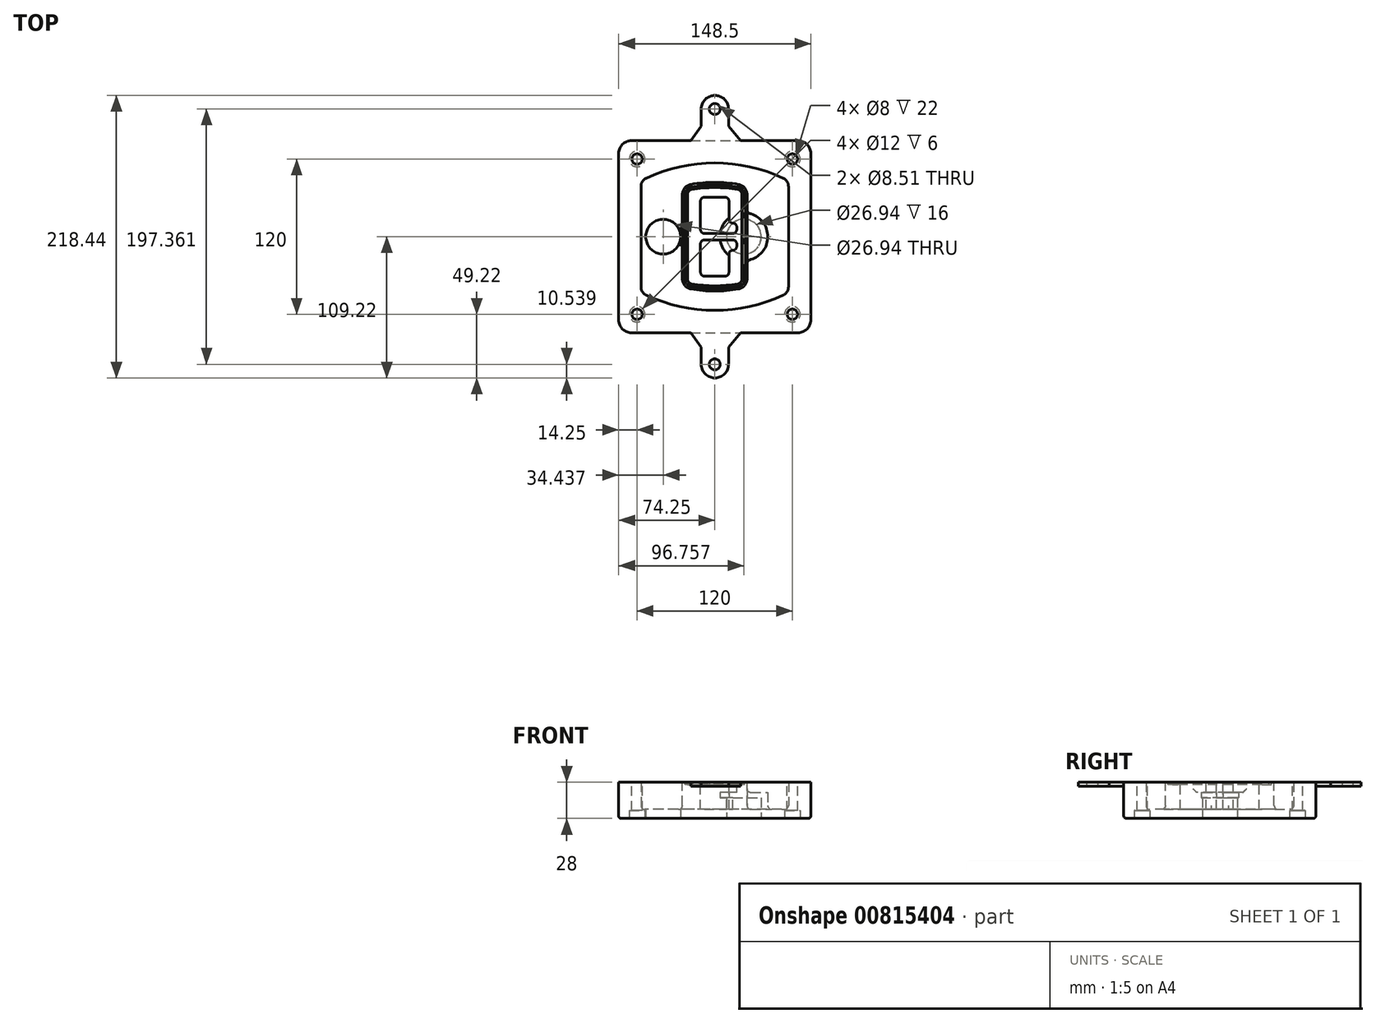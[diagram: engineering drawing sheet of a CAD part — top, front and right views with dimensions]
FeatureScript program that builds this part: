
annotation { "Feature Type Name" : "Feature", "Feature Type Description" : "" }
export const myFeature = defineFeature(function(context is Context, id is Id, definition is map)
    precondition{}
    {
        {
            var Q0;
            Q0=qCreatedBy(makeId("Top.planeOp"),FACE);
            var sketch = newSketch(context, id + "F0", { "sketchPlane" : qUnion([Q0])});
            skPoint(sketch, "E0.rect.middle", {"position": v(0, 0) * mm});
            skLineSegment(sketch, "E1.bottom", {"start": v(-64.25, -74.25) * mm, "end": v(64.25, -74.25) * mm});
            skLineSegment(sketch, "E1.top", {"start": v(-64.25, 74.25) * mm, "end": v(64.25, 74.25) * mm});
            skLineSegment(sketch, "E1.left", {"start": v(-74.25, -64.25) * mm, "end": v(-74.25, 64.25) * mm});
            skLineSegment(sketch, "E1.right", {"start": v(74.25, -64.25) * mm, "end": v(74.25, 64.25) * mm});
            skLineSegment(sketch, "E2", {"start": v(-74.25, 74.25) * mm, "end": v(74.25, -74.25) * mm, "construction": true});
            skLineSegment(sketch, "E3", {"start": v(74.25, 74.25) * mm, "end": v(-74.25, -74.25) * mm, "construction": true});
            skCircle(sketch, "E4", {"center": v(-60, 60) * mm, "radius": 4 * mm});
            skCircle(sketch, "E5", {"center": v(60, 60) * mm, "radius": 4 * mm});
            skCircle(sketch, "E6", {"center": v(60, -60) * mm, "radius": 4 * mm});
            skCircle(sketch, "E7", {"center": v(-60, -60) * mm, "radius": 4 * mm});
            skLineSegment(sketch, "E8", {"start": v(-60, 60) * mm, "end": v(60, 60) * mm, "construction": true});
            skLineSegment(sketch, "E9", {"start": v(60, 60) * mm, "end": v(60, -60) * mm, "construction": true});
            skLineSegment(sketch, "E10", {"start": v(60, -60) * mm, "end": v(-60, -60) * mm, "construction": true});
            skLineSegment(sketch, "E11", {"start": v(-60, -60) * mm, "end": v(-60, 60) * mm, "construction": true});
            skLineSegment(sketch, "E12", {"start": v(-60, 38.83) * mm, "end": v(-60, -38.83) * mm});
            skLineSegment(sketch, "E13", {"start": v(60, 38.83) * mm, "end": v(60, -38.83) * mm});
            skArc(sketch, "E14", {"start": v(54.26, 47.88) * mm, "mid": v(0, 60) * mm, "end": v(-54.26, 47.88) * mm});
            skArc(sketch, "E15", {"start": v(-54.26, -47.88) * mm, "mid": v(0, -60) * mm, "end": v(54.26, -47.88) * mm});
            skLineSegment(sketch, "E16", {"start": v(-60, 0) * mm, "end": v(60, 0) * mm, "construction": true});
            skPoint(sketch, "E17.visualSharp", {"position": v(-60, -45) * mm});
            skArc(sketch, "E17.filletArc", {"start": v(-60, -38.83) * mm, "mid": v(-58.44, -44.2) * mm, "end": v(-54.26, -47.88) * mm});
            skPoint(sketch, "E18.visualSharp", {"position": v(-60, 45) * mm});
            skArc(sketch, "E18.filletArc", {"start": v(-54.26, 47.88) * mm, "mid": v(-58.44, 44.2) * mm, "end": v(-60, 38.83) * mm});
            skPoint(sketch, "E19.visualSharp", {"position": v(60, 45) * mm});
            skArc(sketch, "E19.filletArc", {"start": v(60, 38.83) * mm, "mid": v(58.44, 44.2) * mm, "end": v(54.26, 47.88) * mm});
            skPoint(sketch, "E20.visualSharp", {"position": v(60, -45) * mm});
            skArc(sketch, "E20.filletArc", {"start": v(54.26, -47.88) * mm, "mid": v(58.44, -44.2) * mm, "end": v(60, -38.83) * mm});
            skPoint(sketch, "E21.visualSharp", {"position": v(-74.25, 74.25) * mm});
            skArc(sketch, "E21.filletArc", {"start": v(-64.25, 74.25) * mm, "mid": v(-71.32, 71.32) * mm, "end": v(-74.25, 64.25) * mm});
            skPoint(sketch, "E22.visualSharp", {"position": v(74.25, 74.25) * mm});
            skArc(sketch, "E22.filletArc", {"start": v(74.25, 64.25) * mm, "mid": v(71.32, 71.32) * mm, "end": v(64.25, 74.25) * mm});
            skPoint(sketch, "E23.visualSharp", {"position": v(74.25, -74.25) * mm});
            skArc(sketch, "E23.filletArc", {"start": v(64.25, -74.25) * mm, "mid": v(71.32, -71.32) * mm, "end": v(74.25, -64.25) * mm});
            skPoint(sketch, "E24.visualSharp", {"position": v(-74.25, -74.25) * mm});
            skArc(sketch, "E24.filletArc", {"start": v(-74.25, -64.25) * mm, "mid": v(-71.32, -71.32) * mm, "end": v(-64.25, -74.25) * mm});
            skArc(sketch, "E25.0", {"start": v(57, 38.83) * mm, "mid": v(55.9, 42.58) * mm, "end": v(52.98, 45.17) * mm});
            skLineSegment(sketch, "E25.1", {"start": v(57, 38.83) * mm, "end": v(57, -38.83) * mm});
            skArc(sketch, "E25.2", {"start": v(52.98, -45.17) * mm, "mid": v(55.9, -42.58) * mm, "end": v(57, -38.83) * mm});
            skArc(sketch, "E25.3", {"start": v(-52.98, -45.17) * mm, "mid": v(0, -57) * mm, "end": v(52.98, -45.17) * mm});
            skArc(sketch, "E25.4", {"start": v(-57, -38.83) * mm, "mid": v(-55.9, -42.58) * mm, "end": v(-52.98, -45.17) * mm});
            skArc(sketch, "E25.5", {"start": v(52.98, 45.17) * mm, "mid": v(0, 57) * mm, "end": v(-52.98, 45.17) * mm});
            skLineSegment(sketch, "E25.6", {"start": v(-57, 38.83) * mm, "end": v(-57, -38.83) * mm});
            skArc(sketch, "E25.7", {"start": v(-52.98, 45.17) * mm, "mid": v(-55.9, 42.58) * mm, "end": v(-57, 38.83) * mm});
            skArc(sketch, "E26.0", {"start": v(-55.96, 51.5) * mm, "mid": v(-61.82, 46.33) * mm, "end": v(-64, 38.83) * mm});
            skArc(sketch, "E26.1", {"start": v(55.96, 51.5) * mm, "mid": v(0, 64) * mm, "end": v(-55.96, 51.5) * mm});
            skArc(sketch, "E26.2", {"start": v(64, 38.83) * mm, "mid": v(61.82, 46.33) * mm, "end": v(55.96, 51.5) * mm});
            skLineSegment(sketch, "E26.3", {"start": v(64, 38.83) * mm, "end": v(64, -38.83) * mm});
            skArc(sketch, "E26.4", {"start": v(55.96, -51.5) * mm, "mid": v(61.82, -46.33) * mm, "end": v(64, -38.83) * mm});
            skLineSegment(sketch, "E26.5", {"start": v(-64, 38.83) * mm, "end": v(-64, -38.83) * mm});
            skArc(sketch, "E26.6", {"start": v(-55.96, -51.5) * mm, "mid": v(0, -64) * mm, "end": v(55.96, -51.5) * mm});
            skArc(sketch, "E26.7", {"start": v(-64, -38.83) * mm, "mid": v(-61.82, -46.33) * mm, "end": v(-55.96, -51.5) * mm});
            skSolve(sketch);
        }
        {
            var Q0;
            Q0=makeQuery(id+"F0.imprint","IMPRINT",FACE,{"disambiguationData":[TD([[makeQuery(id+"F0.imprint","IMPRINT",EDGE,{"derivedFrom":sQuery(id+"F0.wireOp",EDGE,"E1.bottom")}),1.0]])]});
            var Q1;
            Q1=makeQuery(id+"F0.imprint","IMPRINT",FACE,{"disambiguationData":[TD([[makeQuery(id+"F0.imprint","IMPRINT",EDGE,{"derivedFrom":sQuery(id+"F0.wireOp",EDGE,"E12")}),1.0]])]});
            var Q2;
            Q2=makeQuery(id+"F0.imprint","IMPRINT",FACE,{"disambiguationData":[TD([[makeQuery(id+"F0.imprint","IMPRINT",EDGE,{"derivedFrom":sQuery(id+"F0.wireOp",EDGE,"E25.0")}),1.0]])]});
            var Q3;
            Q3=makeQuery(id+"F0.imprint","IMPRINT",FACE,{"disambiguationData":[TD([[makeQuery(id+"F0.imprint","IMPRINT",EDGE,{"derivedFrom":sQuery(id+"F0.wireOp",EDGE,"E12")}),-1.0]])]});
            extrude(context, id + "F1", {"entities" : qUnion([Q0, Q1, Q2, Q3]), "oppositeDirection" : true, "depth" : 25 * mm, "offsetDistance" : 25 * mm});
        }
        {
            var Q0;
            Q0=makeQuery(id+"F0.imprint","IMPRINT",FACE,{"disambiguationData":[TD([[makeQuery(id+"F0.imprint","IMPRINT",EDGE,{"derivedFrom":sQuery(id+"F0.wireOp",EDGE,"E12")}),1.0]])]});
            extrude(context, id + "F2", {"entities" : qUnion([Q0]), "operationType" : NewBodyOperationType.ADD, "depth" : 3 * mm});
        }
        {
            var Q0;
            Q0=makeQuery(id+"F0.imprint","IMPRINT",FACE,{"disambiguationData":[TD([[makeQuery(id+"F0.imprint","IMPRINT",EDGE,{"derivedFrom":sQuery(id+"F0.wireOp",EDGE,"E25.0")}),1.0]])]});
            extrude(context, id + "F3", {"entities" : qUnion([Q0]), "operationType" : NewBodyOperationType.REMOVE, "oppositeDirection" : true, "depth" : 18 * mm});
        }
        {
            var Q0;
            Q0=makeQuery(id+"F2.opExtrude","CAP_FACE",FACE,{"disambiguationData":[OSD([sQuery(id+"F0.wireOp",EDGE,"E12"),sQuery(id+"F0.wireOp",EDGE,"E13"),sQuery(id+"F0.wireOp",EDGE,"E14"),sQuery(id+"F0.wireOp",EDGE,"E15"),sQuery(id+"F0.wireOp",EDGE,"E17.filletArc"),sQuery(id+"F0.wireOp",EDGE,"E18.filletArc"),sQuery(id+"F0.wireOp",EDGE,"E19.filletArc"),sQuery(id+"F0.wireOp",EDGE,"E20.filletArc"),sQuery(id+"F0.wireOp",EDGE,"E25.0"),sQuery(id+"F0.wireOp",EDGE,"E25.1"),sQuery(id+"F0.wireOp",EDGE,"E25.2"),sQuery(id+"F0.wireOp",EDGE,"E25.3"),sQuery(id+"F0.wireOp",EDGE,"E25.4"),sQuery(id+"F0.wireOp",EDGE,"E25.5"),sQuery(id+"F0.wireOp",EDGE,"E25.6"),sQuery(id+"F0.wireOp",EDGE,"E25.7")])],"isStart":false});
            var sketch = newSketch(context, id + "F4", { "sketchPlane" : qUnion([Q0])});
            skArc(sketch, "E27.0", {"start": v(-18.34, -40.45) * mm, "mid": v(0, -42) * mm, "end": v(18.34, -40.45) * mm});
            skArc(sketch, "E28.0", {"start": v(18.34, 40.45) * mm, "mid": v(0, 42) * mm, "end": v(-18.34, 40.45) * mm});
            skLineSegment(sketch, "E29", {"start": v(-25, 32.57) * mm, "end": v(-25, -32.57) * mm});
            skLineSegment(sketch, "E30", {"start": v(25, 32.57) * mm, "end": v(25, -32.57) * mm});
            skLineSegment(sketch, "E31", {"start": v(-25, 39.1) * mm, "end": v(25, 39.1) * mm, "construction": true});
            skLineSegment(sketch, "E32", {"start": v(-25, -39.1) * mm, "end": v(25, -39.1) * mm, "construction": true});
            skPoint(sketch, "E33.visualSharp", {"position": v(-25, 39.1) * mm});
            skArc(sketch, "E33.filletArc", {"start": v(-18.34, 40.45) * mm, "mid": v(-23.11, 37.73) * mm, "end": v(-25, 32.57) * mm});
            skPoint(sketch, "E34.visualSharp", {"position": v(25, 39.1) * mm});
            skArc(sketch, "E34.filletArc", {"start": v(25, 32.57) * mm, "mid": v(23.11, 37.73) * mm, "end": v(18.34, 40.45) * mm});
            skPoint(sketch, "E35.visualSharp", {"position": v(25, -39.1) * mm});
            skArc(sketch, "E35.filletArc", {"start": v(18.34, -40.45) * mm, "mid": v(23.11, -37.73) * mm, "end": v(25, -32.57) * mm});
            skPoint(sketch, "E36.visualSharp", {"position": v(-25, -39.1) * mm});
            skArc(sketch, "E36.filletArc", {"start": v(-25, -32.57) * mm, "mid": v(-23.11, -37.73) * mm, "end": v(-18.34, -40.45) * mm});
            skArc(sketch, "E37.0", {"start": v(52.98, 45.17) * mm, "mid": v(0, 57) * mm, "end": v(-52.98, 45.17) * mm});
            skArc(sketch, "E37.1", {"start": v(-52.98, 45.17) * mm, "mid": v(-55.9, 42.58) * mm, "end": v(-57, 38.83) * mm});
            skLineSegment(sketch, "E37.2", {"start": v(-57, 38.83) * mm, "end": v(-57, -38.83) * mm});
            skArc(sketch, "E37.3", {"start": v(-57, -38.83) * mm, "mid": v(-55.9, -42.58) * mm, "end": v(-52.98, -45.17) * mm});
            skArc(sketch, "E37.4", {"start": v(-52.98, -45.17) * mm, "mid": v(0, -57) * mm, "end": v(52.98, -45.17) * mm});
            skArc(sketch, "E37.5", {"start": v(52.98, -45.17) * mm, "mid": v(55.9, -42.58) * mm, "end": v(57, -38.83) * mm});
            skLineSegment(sketch, "E37.6", {"start": v(57, 38.83) * mm, "end": v(57, -38.83) * mm});
            skArc(sketch, "E37.7", {"start": v(57, 38.83) * mm, "mid": v(55.9, 42.58) * mm, "end": v(52.98, 45.17) * mm});
            skLineSegment(sketch, "E38.0", {"start": v(23, 32.57) * mm, "end": v(23, -32.57) * mm});
            skArc(sketch, "E38.1", {"start": v(18, -38.48) * mm, "mid": v(21.58, -36.44) * mm, "end": v(23, -32.57) * mm});
            skArc(sketch, "E38.2", {"start": v(-18, -38.48) * mm, "mid": v(0, -40) * mm, "end": v(18, -38.48) * mm});
            skArc(sketch, "E38.3", {"start": v(-23, -32.57) * mm, "mid": v(-21.58, -36.44) * mm, "end": v(-18, -38.48) * mm});
            skLineSegment(sketch, "E38.4", {"start": v(-23, 32.57) * mm, "end": v(-23, -32.57) * mm});
            skArc(sketch, "E38.5", {"start": v(23, 32.57) * mm, "mid": v(21.58, 36.44) * mm, "end": v(18, 38.48) * mm});
            skArc(sketch, "E38.6", {"start": v(-18, 38.48) * mm, "mid": v(-21.58, 36.44) * mm, "end": v(-23, 32.57) * mm});
            skArc(sketch, "E38.7", {"start": v(18, 38.48) * mm, "mid": v(0, 40) * mm, "end": v(-18, 38.48) * mm});
            skArc(sketch, "E39.0", {"start": v(21, 32.57) * mm, "mid": v(20.06, 35.15) * mm, "end": v(17.67, 36.5) * mm});
            skLineSegment(sketch, "E39.1", {"start": v(21, 32.57) * mm, "end": v(21, -32.57) * mm});
            skArc(sketch, "E39.2", {"start": v(17.67, -36.5) * mm, "mid": v(20.06, -35.15) * mm, "end": v(21, -32.57) * mm});
            skArc(sketch, "E39.3", {"start": v(-17.67, -36.5) * mm, "mid": v(0, -38) * mm, "end": v(17.67, -36.5) * mm});
            skArc(sketch, "E39.4", {"start": v(-21, -32.57) * mm, "mid": v(-20.06, -35.15) * mm, "end": v(-17.67, -36.5) * mm});
            skArc(sketch, "E39.5", {"start": v(17.67, 36.5) * mm, "mid": v(0, 38) * mm, "end": v(-17.67, 36.5) * mm});
            skLineSegment(sketch, "E39.6", {"start": v(-21, 32.57) * mm, "end": v(-21, -32.57) * mm});
            skArc(sketch, "E39.7", {"start": v(-17.67, 36.5) * mm, "mid": v(-20.06, 35.15) * mm, "end": v(-21, 32.57) * mm});
            skLineSegment(sketch, "E40", {"start": v(-25, 0) * mm, "end": v(25, 0) * mm, "construction": true});
            skLineSegment(sketch, "E41", {"start": v(-11, 5.5) * mm, "end": v(-11, 27.5) * mm});
            skLineSegment(sketch, "E42", {"start": v(-8, 30.5) * mm, "end": v(8, 30.5) * mm});
            skLineSegment(sketch, "E43", {"start": v(11, 27.5) * mm, "end": v(11, 13.5) * mm});
            skLineSegment(sketch, "E44", {"start": v(14, 10.5) * mm, "end": v(14, 10.5) * mm});
            skLineSegment(sketch, "E45", {"start": v(17, 7.5) * mm, "end": v(17, 5.5) * mm});
            skLineSegment(sketch, "E46", {"start": v(14, 2.5) * mm, "end": v(-8, 2.5) * mm});
            skPoint(sketch, "E47.visualSharp", {"position": v(-11, 30.5) * mm});
            skArc(sketch, "E47.filletArc", {"start": v(-8, 30.5) * mm, "mid": v(-10.12, 29.62) * mm, "end": v(-11, 27.5) * mm});
            skPoint(sketch, "E48.visualSharp", {"position": v(11, 30.5) * mm});
            skArc(sketch, "E48.filletArc", {"start": v(11, 27.5) * mm, "mid": v(10.12, 29.62) * mm, "end": v(8, 30.5) * mm});
            skPoint(sketch, "E49.visualSharp", {"position": v(11, 10.5) * mm});
            skArc(sketch, "E49.filletArc", {"start": v(11, 13.5) * mm, "mid": v(11.88, 11.38) * mm, "end": v(14, 10.5) * mm});
            skPoint(sketch, "E50.visualSharp", {"position": v(17, 10.5) * mm});
            skArc(sketch, "E50.filletArc", {"start": v(17, 7.5) * mm, "mid": v(16.12, 9.62) * mm, "end": v(14, 10.5) * mm});
            skPoint(sketch, "E51.visualSharp", {"position": v(17, 2.5) * mm});
            skArc(sketch, "E51.filletArc", {"start": v(14, 2.5) * mm, "mid": v(16.12, 3.38) * mm, "end": v(17, 5.5) * mm});
            skPoint(sketch, "E52.visualSharp", {"position": v(-11, 2.5) * mm});
            skArc(sketch, "E52.filletArc", {"start": v(-11, 5.5) * mm, "mid": v(-10.12, 3.38) * mm, "end": v(-8, 2.5) * mm});
            skLineSegment(sketch, "E53.0.MirrorCS", {"start": v(14, -2.5) * mm, "end": v(-8, -2.5) * mm});
            skArc(sketch, "E54.0.MirrorCS", {"start": v(-11, -5.5) * mm, "mid": v(-10.12, -3.38) * mm, "end": v(-8, -2.5) * mm});
            skLineSegment(sketch, "E55.0.MirrorCS", {"start": v(-11, -5.5) * mm, "end": v(-11, -27.5) * mm});
            skArc(sketch, "E56.0.MirrorCS", {"start": v(-8, -30.5) * mm, "mid": v(-10.12, -29.62) * mm, "end": v(-11, -27.5) * mm});
            skLineSegment(sketch, "E57.0.MirrorCS", {"start": v(-8, -30.5) * mm, "end": v(8, -30.5) * mm});
            skArc(sketch, "E58.0.MirrorCS", {"start": v(11, -27.5) * mm, "mid": v(10.12, -29.62) * mm, "end": v(8, -30.5) * mm});
            skLineSegment(sketch, "E59.0.MirrorCS", {"start": v(11, -27.5) * mm, "end": v(11, -13.5) * mm});
            skArc(sketch, "E60.0.MirrorCS", {"start": v(11, -13.5) * mm, "mid": v(11.88, -11.38) * mm, "end": v(14, -10.5) * mm});
            skArc(sketch, "E61.0.MirrorCS", {"start": v(17, -7.5) * mm, "mid": v(16.12, -9.62) * mm, "end": v(14, -10.5) * mm});
            skLineSegment(sketch, "E62.0.MirrorCS", {"start": v(17, -7.5) * mm, "end": v(17, -5.5) * mm});
            skArc(sketch, "E63.0.MirrorCS", {"start": v(14, -2.5) * mm, "mid": v(16.12, -3.38) * mm, "end": v(17, -5.5) * mm});
            skSolve(sketch);
        }
        {
            var Q0;
            Q0=makeQuery(id+"F4.imprint","IMPRINT",FACE,{"disambiguationData":[TD([[makeQuery(id+"F4.imprint","IMPRINT",EDGE,{"derivedFrom":sQuery(id+"F4.wireOp",EDGE,"E27.0")}),1.0]])]});
            var Q1;
            Q1=makeQuery(id+"F4.imprint","IMPRINT",FACE,{"disambiguationData":[TD([[makeQuery(id+"F4.imprint","IMPRINT",EDGE,{"derivedFrom":sQuery(id+"F4.wireOp",EDGE,"E38.0")}),-1.0]])]});
            var Q2;
            Q2=makeQuery(id+"F4.imprint","IMPRINT",FACE,{"disambiguationData":[TD([[makeQuery(id+"F4.imprint","IMPRINT",EDGE,{"derivedFrom":sQuery(id+"F4.wireOp",EDGE,"E39.0")}),1.0]])]});
            extrude(context, id + "F5", {"entities" : qUnion([Q0, Q1, Q2]), "operationType" : NewBodyOperationType.ADD, "endBound" : BoundingType.UP_TO_NEXT, "oppositeDirection" : true, "depth" : 25 * mm, "offsetDistance" : 25 * mm});
        }
        {
            var Q0;
            Q0=makeQuery(id+"F4.imprint","IMPRINT",FACE,{"disambiguationData":[TD([[makeQuery(id+"F4.imprint","IMPRINT",EDGE,{"derivedFrom":sQuery(id+"F4.wireOp",EDGE,"E38.0")}),-1.0]])]});
            extrude(context, id + "F6", {"entities" : qUnion([Q0]), "operationType" : NewBodyOperationType.REMOVE, "oppositeDirection" : true, "depth" : 2 * mm});
        }
        {
            var Q0;
            Q0=makeQuery(id+"F1.opExtrude","CAP_FACE",FACE,{"disambiguationData":[OSD([sQuery(id+"F0.wireOp",EDGE,"E1.bottom"),sQuery(id+"F0.wireOp",EDGE,"E1.top"),sQuery(id+"F0.wireOp",EDGE,"E1.left"),sQuery(id+"F0.wireOp",EDGE,"E1.right"),sQuery(id+"F0.wireOp",EDGE,"E4"),sQuery(id+"F0.wireOp",EDGE,"E5"),sQuery(id+"F0.wireOp",EDGE,"E6"),sQuery(id+"F0.wireOp",EDGE,"E7"),sQuery(id+"F0.wireOp",EDGE,"E21.filletArc"),sQuery(id+"F0.wireOp",EDGE,"E22.filletArc"),sQuery(id+"F0.wireOp",EDGE,"E23.filletArc"),sQuery(id+"F0.wireOp",EDGE,"E24.filletArc")])],"isStart":false});
            var sketch = newSketch(context, id + "F7", { "sketchPlane" : qUnion([Q0])});
            skCircle(sketch, "E64", {"center": v(22.5, 0) * mm, "radius": 13.47 * mm});
            skCircle(sketch, "E65", {"center": v(-39.81, 0) * mm, "radius": 13.47 * mm});
            skLineSegment(sketch, "E66", {"start": v(74.25, 0) * mm, "end": v(-74.25, 0) * mm});
            skCircle(sketch, "E67", {"center": v(22.5, 0) * mm, "radius": 18.47 * mm});
            skCircle(sketch, "E68", {"center": v(60, -60) * mm, "radius": 6 * mm});
            skCircle(sketch, "E69", {"center": v(-60, -60) * mm, "radius": 6 * mm});
            skCircle(sketch, "E70", {"center": v(-60, 60) * mm, "radius": 6 * mm});
            skCircle(sketch, "E71", {"center": v(60, 60) * mm, "radius": 6 * mm});
            skSolve(sketch);
        }
        {
            var Q0;
            {var subQ1=sQuery(id+"F7.wireOp",EDGE,"E66");var subQ4=sQuery(id+"F7.wireOp",EDGE,"E64");var subQ6=makeQuery(id+"F7.imprint","INTERSECT",VERTEX,{"disambiguationData":[OD(0.0)],"derivedFrom":[subQ4,subQ1]});Q0=makeQuery(id+"F7.imprint","IMPRINT",FACE,{"disambiguationData":[TD([[makeQuery(id+"F7.imprint","IMPRINT",EDGE,{"disambiguationData":[TD([[subQ6,-1.0]])],"derivedFrom":subQ4}),-1.0]])]});}
            var Q1;
            {var subQ0=sQuery(id+"F7.wireOp",EDGE,"E66");var subQ1=sQuery(id+"F7.wireOp",EDGE,"E64");var subQ3=makeQuery(id+"F7.imprint","INTERSECT",VERTEX,{"disambiguationData":[OD(0.0)],"derivedFrom":[subQ1,subQ0]});Q1=makeQuery(id+"F7.imprint","IMPRINT",FACE,{"disambiguationData":[TD([[makeQuery(id+"F7.imprint","IMPRINT",EDGE,{"disambiguationData":[TD([[subQ3,-1.0]])],"derivedFrom":subQ1}),1.0]])]});}
            var Q2;
            {var subQ0=sQuery(id+"F7.wireOp",EDGE,"E66");var subQ1=sQuery(id+"F7.wireOp",EDGE,"E64");var subQ3=makeQuery(id+"F7.imprint","INTERSECT",VERTEX,{"disambiguationData":[OD(0.0)],"derivedFrom":[subQ1,subQ0]});Q2=makeQuery(id+"F7.imprint","IMPRINT",FACE,{"disambiguationData":[TD([[makeQuery(id+"F7.imprint","IMPRINT",EDGE,{"disambiguationData":[TD([[subQ3,1.0]])],"derivedFrom":subQ1}),1.0]])]});}
            var Q3;
            {var subQ1=sQuery(id+"F7.wireOp",EDGE,"E66");var subQ4=sQuery(id+"F7.wireOp",EDGE,"E64");var subQ6=makeQuery(id+"F7.imprint","INTERSECT",VERTEX,{"disambiguationData":[OD(0.0)],"derivedFrom":[subQ4,subQ1]});Q3=makeQuery(id+"F7.imprint","IMPRINT",FACE,{"disambiguationData":[TD([[makeQuery(id+"F7.imprint","IMPRINT",EDGE,{"disambiguationData":[TD([[subQ6,1.0]])],"derivedFrom":subQ4}),-1.0]])]});}
            extrude(context, id + "F8", {"entities" : qUnion([Q0, Q1, Q2, Q3]), "operationType" : NewBodyOperationType.ADD, "oppositeDirection" : true, "depth" : 20 * mm});
        }
        {
            var Q0;
            {var subQ0=sQuery(id+"F7.wireOp",EDGE,"E66");var subQ1=sQuery(id+"F7.wireOp",EDGE,"E64");var subQ3=makeQuery(id+"F7.imprint","INTERSECT",VERTEX,{"disambiguationData":[OD(0.0)],"derivedFrom":[subQ1,subQ0]});Q0=makeQuery(id+"F7.imprint","IMPRINT",FACE,{"disambiguationData":[TD([[makeQuery(id+"F7.imprint","IMPRINT",EDGE,{"disambiguationData":[TD([[subQ3,-1.0]])],"derivedFrom":subQ1}),1.0]])]});}
            var Q1;
            {var subQ0=sQuery(id+"F7.wireOp",EDGE,"E66");var subQ1=sQuery(id+"F7.wireOp",EDGE,"E64");var subQ3=makeQuery(id+"F7.imprint","INTERSECT",VERTEX,{"disambiguationData":[OD(0.0)],"derivedFrom":[subQ1,subQ0]});Q1=makeQuery(id+"F7.imprint","IMPRINT",FACE,{"disambiguationData":[TD([[makeQuery(id+"F7.imprint","IMPRINT",EDGE,{"disambiguationData":[TD([[subQ3,1.0]])],"derivedFrom":subQ1}),1.0]])]});}
            extrude(context, id + "F9", {"entities" : qUnion([Q0, Q1]), "operationType" : NewBodyOperationType.REMOVE, "oppositeDirection" : true, "depth" : 16 * mm});
        }
        {
            var Q0;
            {var subQ0=sQuery(id+"F7.wireOp",EDGE,"E66");var subQ1=sQuery(id+"F7.wireOp",EDGE,"E65");var subQ3=makeQuery(id+"F7.imprint","INTERSECT",VERTEX,{"disambiguationData":[OD(0.0)],"derivedFrom":[subQ1,subQ0]});Q0=makeQuery(id+"F7.imprint","IMPRINT",FACE,{"disambiguationData":[TD([[makeQuery(id+"F7.imprint","IMPRINT",EDGE,{"disambiguationData":[TD([[subQ3,-1.0]])],"derivedFrom":subQ1}),1.0]])]});}
            var Q1;
            {var subQ0=sQuery(id+"F7.wireOp",EDGE,"E66");var subQ1=sQuery(id+"F7.wireOp",EDGE,"E65");var subQ3=makeQuery(id+"F7.imprint","INTERSECT",VERTEX,{"disambiguationData":[OD(0.0)],"derivedFrom":[subQ1,subQ0]});Q1=makeQuery(id+"F7.imprint","IMPRINT",FACE,{"disambiguationData":[TD([[makeQuery(id+"F7.imprint","IMPRINT",EDGE,{"disambiguationData":[TD([[subQ3,1.0]])],"derivedFrom":subQ1}),1.0]])]});}
            extrude(context, id + "F10", {"entities" : qUnion([Q0, Q1]), "operationType" : NewBodyOperationType.REMOVE, "oppositeDirection" : true, "depth" : 25 * mm, "offsetDistance" : 25 * mm});
        }
        {
            var Q0;
            Q0=makeQuery(id+"F7.imprint","IMPRINT",FACE,{"disambiguationData":[TD([[makeQuery(id+"F7.imprint","IMPRINT",EDGE,{"derivedFrom":sQuery(id+"F7.wireOp",EDGE,"E68")}),1.0]])]});
            var Q1;
            Q1=makeQuery(id+"F7.imprint","IMPRINT",FACE,{"disambiguationData":[TD([[makeQuery(id+"F7.imprint","IMPRINT",EDGE,{"derivedFrom":makeQuery(id+"F1.opExtrude","CAP_EDGE",EDGE,{"disambiguationData":[OSD([sQuery(id+"F0.wireOp",EDGE,"E5")])],"isStart":false})}),-1.0]])]});
            var Q2;
            Q2=makeQuery(id+"F7.imprint","IMPRINT",FACE,{"disambiguationData":[TD([[makeQuery(id+"F7.imprint","IMPRINT",EDGE,{"derivedFrom":sQuery(id+"F7.wireOp",EDGE,"E69")}),1.0]])]});
            var Q3;
            Q3=makeQuery(id+"F7.imprint","IMPRINT",FACE,{"disambiguationData":[TD([[makeQuery(id+"F7.imprint","IMPRINT",EDGE,{"derivedFrom":makeQuery(id+"F1.opExtrude","CAP_EDGE",EDGE,{"disambiguationData":[OSD([sQuery(id+"F0.wireOp",EDGE,"E4")])],"isStart":false})}),-1.0]])]});
            var Q4;
            Q4=makeQuery(id+"F7.imprint","IMPRINT",FACE,{"disambiguationData":[TD([[makeQuery(id+"F7.imprint","IMPRINT",EDGE,{"derivedFrom":sQuery(id+"F7.wireOp",EDGE,"E70")}),1.0]])]});
            var Q5;
            Q5=makeQuery(id+"F7.imprint","IMPRINT",FACE,{"disambiguationData":[TD([[makeQuery(id+"F7.imprint","IMPRINT",EDGE,{"derivedFrom":makeQuery(id+"F1.opExtrude","CAP_EDGE",EDGE,{"disambiguationData":[OSD([sQuery(id+"F0.wireOp",EDGE,"E7")])],"isStart":false})}),-1.0]])]});
            var Q6;
            Q6=makeQuery(id+"F7.imprint","IMPRINT",FACE,{"disambiguationData":[TD([[makeQuery(id+"F7.imprint","IMPRINT",EDGE,{"derivedFrom":sQuery(id+"F7.wireOp",EDGE,"E71")}),1.0]])]});
            var Q7;
            Q7=makeQuery(id+"F7.imprint","IMPRINT",FACE,{"disambiguationData":[TD([[makeQuery(id+"F7.imprint","IMPRINT",EDGE,{"derivedFrom":makeQuery(id+"F1.opExtrude","CAP_EDGE",EDGE,{"disambiguationData":[OSD([sQuery(id+"F0.wireOp",EDGE,"E6")])],"isStart":false})}),-1.0]])]});
            extrude(context, id + "F11", {"entities" : qUnion([Q0, Q1, Q2, Q3, Q4, Q5, Q6, Q7]), "operationType" : NewBodyOperationType.REMOVE, "oppositeDirection" : true, "depth" : 6 * mm});
        }
        {
            var Q0;
            Q0=makeQuery(id+"F9.boolean.opBoolean","COPY",FACE,{"derivedFrom":makeQuery(id+"F9.opExtrude","CAP_FACE",FACE,{"disambiguationData":[OSD([sQuery(id+"F7.wireOp",EDGE,"E64")])],"isStart":false})});
            var sketch = newSketch(context, id + "F12", { "sketchPlane" : qUnion([Q0])});
            skArc(sketch, "E72.0", {"start": v(11, 14.45) * mm, "mid": v(6.45, 9.13) * mm, "end": v(4.2, 2.5) * mm});
            skArc(sketch, "E72.1", {"start": v(4.2, -2.5) * mm, "mid": v(6.45, -9.13) * mm, "end": v(11, -14.45) * mm});
            skLineSegment(sketch, "E73", {"start": v(4.2, -2.5) * mm, "end": v(14, -2.5) * mm});
            skLineSegment(sketch, "E74.0", {"start": v(14, 2.5) * mm, "end": v(4.2, 2.5) * mm});
            skArc(sketch, "E74.1", {"start": v(14, 2.5) * mm, "mid": v(16.12, 3.38) * mm, "end": v(17, 5.5) * mm});
            skLineSegment(sketch, "E74.2", {"start": v(17, 7.5) * mm, "end": v(17, 5.5) * mm});
            skArc(sketch, "E74.3", {"start": v(17, 7.5) * mm, "mid": v(16.12, 9.62) * mm, "end": v(14, 10.5) * mm});
            skArc(sketch, "E74.4", {"start": v(11, 13.5) * mm, "mid": v(11.88, 11.38) * mm, "end": v(14, 10.5) * mm});
            skLineSegment(sketch, "E74.5", {"start": v(11, 14.45) * mm, "end": v(11, 13.5) * mm});
            skLineSegment(sketch, "E74.7", {"start": v(14, -2.5) * mm, "end": v(4.2, -2.5) * mm});
            skArc(sketch, "E74.8", {"start": v(14, -2.5) * mm, "mid": v(16.12, -3.38) * mm, "end": v(17, -5.5) * mm});
            skLineSegment(sketch, "E74.9", {"start": v(17, -7.5) * mm, "end": v(17, -5.5) * mm});
            skArc(sketch, "E74.10", {"start": v(17, -7.5) * mm, "mid": v(16.12, -9.62) * mm, "end": v(14, -10.5) * mm});
            skArc(sketch, "E74.11", {"start": v(11, -13.5) * mm, "mid": v(11.88, -11.38) * mm, "end": v(14, -10.5) * mm});
            skLineSegment(sketch, "E74.12", {"start": v(11, -14.45) * mm, "end": v(11, -13.5) * mm});
            skPoint(sketch, "E75.orphan", {"position": v(11, -27.5) * mm});
            skPoint(sketch, "E76.orphan", {"position": v(-8, -2.5) * mm});
            skPoint(sketch, "E77.orphan", {"position": v(-8, 2.5) * mm});
            skPoint(sketch, "E78.orphan", {"position": v(11, 27.5) * mm});
            skSolve(sketch);
        }
        {
            var Q0;
            {var subQ7=sQuery(id+"F12.wireOp",EDGE,"E72.0");var subQ14=sQuery(id+"F12.wireOp",EDGE,"E72.1");var subQ16=sQuery(id+"F12.wireOp",EDGE,"E74.1");var subQ18=sQuery(id+"F12.wireOp",EDGE,"E74.8");Q0=qUnion([makeQuery(id+"F12.imprint","IMPRINT",FACE,{"disambiguationData":[TD([[makeQuery(id+"F12.imprint","IMPRINT",EDGE,{"derivedFrom":subQ7}),1.0]])]}),makeQuery(id+"F12.imprint","IMPRINT",FACE,{"disambiguationData":[TD([[makeQuery(id+"F12.imprint","IMPRINT",EDGE,{"derivedFrom":subQ14}),1.0]])]}),makeQuery(id+"F12.imprint","IMPRINT",FACE,{"disambiguationData":[TD([[makeQuery(id+"F12.imprint","IMPRINT",EDGE,{"derivedFrom":subQ16}),1.0]])]}),makeQuery(id+"F12.imprint","IMPRINT",FACE,{"disambiguationData":[TD([[makeQuery(id+"F12.imprint","IMPRINT",EDGE,{"derivedFrom":subQ18}),-1.0]])]})]);}
            var Q1;
            Q1=makeQuery(id+"F5.boolean.opBoolean","SPLIT",FACE,{"disambiguationData":[TD([makeQuery(id+"F5.opExtrude","SWEPT_FACE",FACE,{"disambiguationData":[OSD([sQuery(id+"F4.wireOp",EDGE,"E41")])]})])],"derivedFrom":makeQuery(id+"F3.boolean.opBoolean","COPY",FACE,{"derivedFrom":makeQuery(id+"F3.opExtrude","CAP_FACE",FACE,{"disambiguationData":[OSD([sQuery(id+"F0.wireOp",EDGE,"E25.0"),sQuery(id+"F0.wireOp",EDGE,"E25.1"),sQuery(id+"F0.wireOp",EDGE,"E25.2"),sQuery(id+"F0.wireOp",EDGE,"E25.3"),sQuery(id+"F0.wireOp",EDGE,"E25.4"),sQuery(id+"F0.wireOp",EDGE,"E25.5"),sQuery(id+"F0.wireOp",EDGE,"E25.6"),sQuery(id+"F0.wireOp",EDGE,"E25.7")])],"isStart":false})})});
            extrude(context, id + "F13", {"entities" : qUnion([Q0]), "operationType" : NewBodyOperationType.REMOVE, "endBound" : BoundingType.UP_TO_SURFACE, "endBoundEntityFace" : qUnion([Q1]), "depth" : 25 * mm});
        }
        {
            var Q0;
            Q0=makeQuery(id+"F3.boolean.opBoolean","COPY",EDGE,{"derivedFrom":makeQuery(id+"F3.opExtrude","CAP_EDGE",EDGE,{"disambiguationData":[OSD([sQuery(id+"F0.wireOp",EDGE,"E25.6")])],"isStart":false})});
            var Q1;
            Q1=makeQuery(id+"F8.boolean.opBoolean","INTERSECT",EDGE,{"derivedFrom":[makeQuery(id+"F5.opExtrude","SWEPT_FACE",FACE,{"disambiguationData":[OSD([sQuery(id+"F4.wireOp",EDGE,"E30")])]}),makeQuery(id+"F8.opExtrude","CAP_FACE",FACE,{"disambiguationData":[OSD([sQuery(id+"F7.wireOp",EDGE,"E67")])],"isStart":false})]});
            var Q2;
            Q2=makeQuery(id+"F8.boolean.opBoolean","INTERSECT",EDGE,{"disambiguationData":[OD(1.0)],"derivedFrom":[makeQuery(id+"F5.opExtrude","SWEPT_FACE",FACE,{"disambiguationData":[OSD([sQuery(id+"F4.wireOp",EDGE,"E30")])]}),makeQuery(id+"F8.opExtrude","SWEPT_FACE",FACE,{"disambiguationData":[OSD([sQuery(id+"F7.wireOp",EDGE,"E67")])]})]});
            var Q3;
            {var subQ0=sQuery(id+"F4.wireOp",EDGE,"E30");Q3=makeQuery(id+"F8.boolean.opBoolean","SPLIT",EDGE,{"disambiguationData":[TD([makeQuery(id+"F5.opExtrude","SWEPT_FACE",FACE,{"disambiguationData":[OSD([sQuery(id+"F4.wireOp",EDGE,"E35.filletArc")])]})])],"derivedFrom":makeQuery(id+"F5.opExtrude","CAP_EDGE",EDGE,{"disambiguationData":[OSD([subQ0])],"isStart":false})});}
            var Q4;
            {var subQ0=sQuery(id+"F0.wireOp",EDGE,"E25.7");var subQ1=sQuery(id+"F0.wireOp",EDGE,"E25.1");var subQ2=sQuery(id+"F0.wireOp",EDGE,"E25.6");var subQ3=sQuery(id+"F0.wireOp",EDGE,"E25.5");var subQ4=sQuery(id+"F0.wireOp",EDGE,"E25.4");var subQ5=sQuery(id+"F0.wireOp",EDGE,"E25.0");var subQ6=sQuery(id+"F0.wireOp",EDGE,"E25.2");var subQ7=sQuery(id+"F0.wireOp",EDGE,"E25.3");Q4=makeQuery(id+"F8.boolean.opBoolean","INTERSECT",EDGE,{"derivedFrom":[makeQuery(id+"F5.boolean.opBoolean","SPLIT",FACE,{"disambiguationData":[TD([makeQuery(id+"F2.opExtrude","SWEPT_FACE",FACE,{"disambiguationData":[OSD([subQ5])]})])],"derivedFrom":makeQuery(id+"F3.boolean.opBoolean","COPY",FACE,{"derivedFrom":makeQuery(id+"F3.opExtrude","CAP_FACE",FACE,{"disambiguationData":[OSD([subQ5,subQ1,subQ6,subQ7,subQ4,subQ3,subQ2,subQ0])],"isStart":false})})}),makeQuery(id+"F8.opExtrude","SWEPT_FACE",FACE,{"disambiguationData":[OSD([sQuery(id+"F7.wireOp",EDGE,"E67")])]})]});}
            var Q5;
            Q5=makeQuery(id+"F8.boolean.opBoolean","INTERSECT",EDGE,{"disambiguationData":[OD(0.0)],"derivedFrom":[makeQuery(id+"F5.opExtrude","SWEPT_FACE",FACE,{"disambiguationData":[OSD([sQuery(id+"F4.wireOp",EDGE,"E30")])]}),makeQuery(id+"F8.opExtrude","SWEPT_FACE",FACE,{"disambiguationData":[OSD([sQuery(id+"F7.wireOp",EDGE,"E67")])]})]});
            fillet(context, id + "F14", {"entities" : qUnion([Q0, Q1, Q2, Q3, Q4, Q5]), "radius" : 3 * mm, "tangentPropagation" : true, "allowEdgeOverflow" : false});
        }
        {
            var Q0;
            Q0=makeQuery(id+"F1.opExtrude","CAP_EDGE",EDGE,{"disambiguationData":[OSD([sQuery(id+"F0.wireOp",EDGE,"E1.bottom")])],"isStart":false});
            fillet(context, id + "F15", {"entities" : qUnion([Q0]), "radius" : 2 * mm, "tangentPropagation" : true, "allowEdgeOverflow" : false});
        }
        {
            var Q0;
            {var subQ0=sQuery(id+"F0.wireOp",EDGE,"E21.filletArc");var subQ1=sQuery(id+"F0.wireOp",EDGE,"E7");var subQ2=sQuery(id+"F0.wireOp",EDGE,"E6");var subQ3=sQuery(id+"F0.wireOp",EDGE,"E5");var subQ4=sQuery(id+"F0.wireOp",EDGE,"E4");var subQ5=sQuery(id+"F0.wireOp",EDGE,"E22.filletArc");var subQ6=sQuery(id+"F0.wireOp",EDGE,"E1.bottom");var subQ7=sQuery(id+"F0.wireOp",EDGE,"E1.right");var subQ8=sQuery(id+"F0.wireOp",EDGE,"E1.top");var subQ9=sQuery(id+"F0.wireOp",EDGE,"E1.left");var subQ10=sQuery(id+"F0.wireOp",EDGE,"E23.filletArc");var subQ11=sQuery(id+"F0.wireOp",EDGE,"E24.filletArc");Q0=makeQuery(id+"F2.boolean.opBoolean","SPLIT",FACE,{"disambiguationData":[TD([makeQuery(id+"F1.opExtrude","SWEPT_FACE",FACE,{"disambiguationData":[OSD([subQ6])]})])],"derivedFrom":makeQuery(id+"F1.opExtrude","CAP_FACE",FACE,{"disambiguationData":[OSD([subQ6,subQ8,subQ9,subQ7,subQ4,subQ3,subQ2,subQ1,subQ0,subQ5,subQ10,subQ11])],"isStart":true})});}
            var sketch = newSketch(context, id + "F16", { "sketchPlane" : qUnion([Q0])});
            skLineSegment(sketch, "E79", {"start": v(0, 74.25) * mm, "end": v(0, 98.68) * mm, "construction": true});
            skLineSegment(sketch, "E80", {"start": v(20, 74.25) * mm, "end": v(10.66, 85.5) * mm});
            skLineSegment(sketch, "E81", {"start": v(-18.56, 74.25) * mm, "end": v(-10.42, 85.5) * mm});
            skLineSegment(sketch, "E82", {"start": v(-10.42, 85.5) * mm, "end": v(-10.42, 98.68) * mm});
            skLineSegment(sketch, "E83", {"start": v(10.66, 85.5) * mm, "end": v(10.66, 98.68) * mm});
            skCircle(sketch, "E84", {"center": v(0, 98.68) * mm, "radius": 4.25 * mm});
            skArc(sketch, "E85", {"start": v(10.66, 98.68) * mm, "mid": v(0.12, 109.22) * mm, "end": v(-10.42, 98.68) * mm});
            skLineSegment(sketch, "E86", {"start": v(74.25, 0) * mm, "end": v(-74.25, 0) * mm});
            skLineSegment(sketch, "E87.MirrorCS", {"start": v(20, -74.25) * mm, "end": v(10.66, -85.5) * mm});
            skLineSegment(sketch, "E88.MirrorCS", {"start": v(10.66, -85.5) * mm, "end": v(10.66, -98.68) * mm});
            skArc(sketch, "E89.MirrorCS", {"start": v(10.66, -98.68) * mm, "mid": v(0.12, -109.22) * mm, "end": v(-10.42, -98.68) * mm});
            skCircle(sketch, "E90.MirrorC", {"center": v(0, -98.68) * mm, "radius": 4.25 * mm});
            skLineSegment(sketch, "E91.MirrorCS", {"start": v(-18.56, -74.25) * mm, "end": v(-10.42, -85.5) * mm});
            skLineSegment(sketch, "E92.MirrorCS", {"start": v(-10.42, -85.5) * mm, "end": v(-10.42, -98.68) * mm});
            skSolve(sketch);
        }
        {
            var Q0;
            Q0=makeQuery(id+"F16.imprint","IMPRINT",FACE,{"disambiguationData":[TD([[makeQuery(id+"F16.imprint","IMPRINT",EDGE,{"derivedFrom":makeQuery(id+"F1.opExtrude","CAP_EDGE",EDGE,{"disambiguationData":[OSD([sQuery(id+"F0.wireOp",EDGE,"E4")])],"isStart":true})}),-1.0]])]});
            var Q1;
            {var subQ1=sQuery(id+"F16.wireOp",EDGE,"E80");Q1=makeQuery(id+"F16.imprint","IMPRINT",FACE,{"disambiguationData":[TD([[makeQuery(id+"F16.imprint","IMPRINT",EDGE,{"derivedFrom":subQ1}),1.0]])]});}
            var Q2;
            Q2=makeQuery(id+"F16.imprint","IMPRINT",FACE,{"disambiguationData":[TD([[makeQuery(id+"F16.imprint","IMPRINT",EDGE,{"derivedFrom":makeQuery(id+"F1.opExtrude","CAP_EDGE",EDGE,{"disambiguationData":[OSD([sQuery(id+"F0.wireOp",EDGE,"E6")])],"isStart":true})}),-1.0]])]});
            var Q3;
            Q3=makeQuery(id+"F16.imprint","IMPRINT",FACE,{"disambiguationData":[TD([[makeQuery(id+"F16.imprint","IMPRINT",EDGE,{"derivedFrom":sQuery(id+"F16.wireOp",EDGE,"E88.MirrorCS")}),-1.0]])]});
            extrude(context, id + "F17", {"entities" : qUnion([Q0, Q1, Q2, Q3]), "operationType" : NewBodyOperationType.ADD, "depth" : 3 * mm, "offsetDistance" : 25 * mm});
        }
    });
